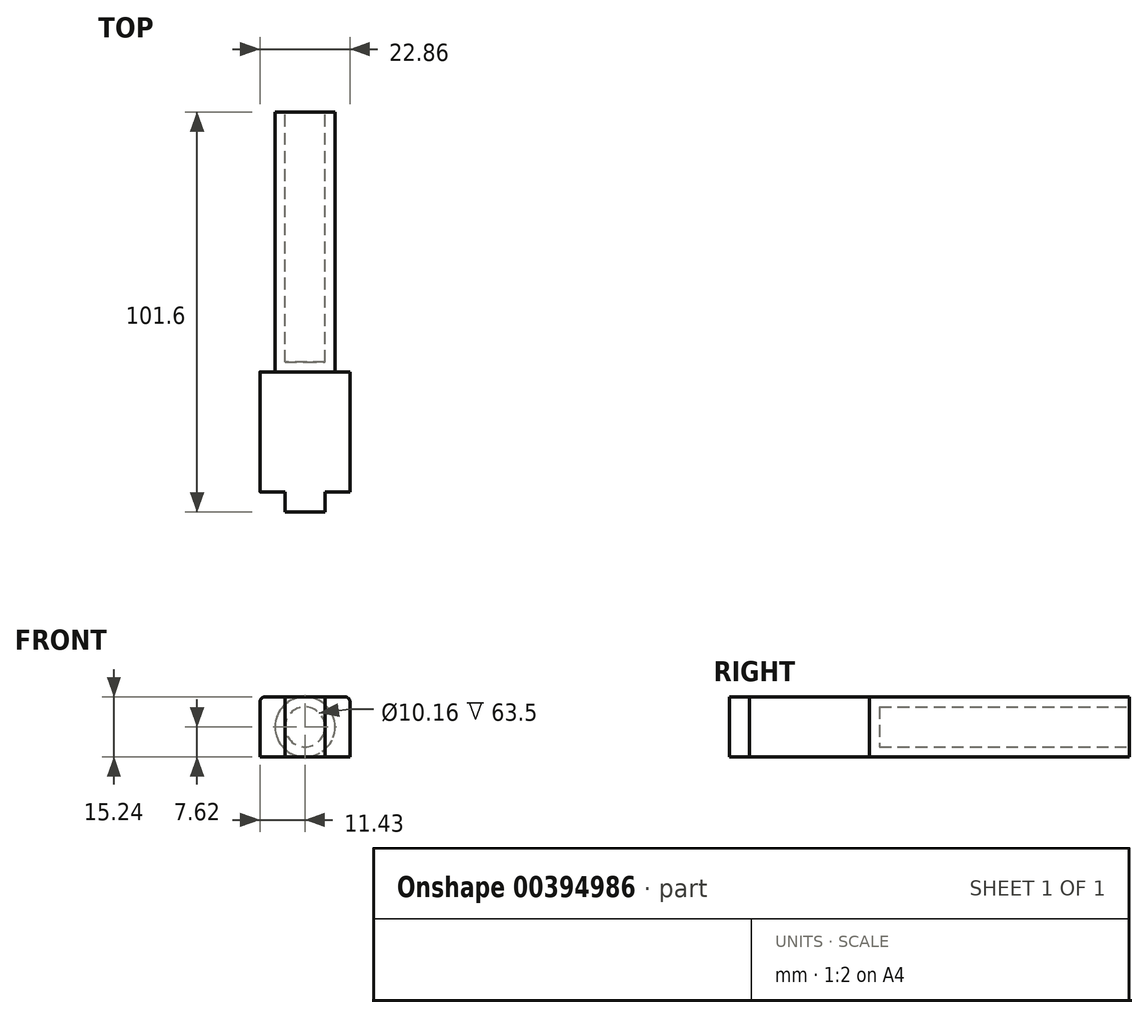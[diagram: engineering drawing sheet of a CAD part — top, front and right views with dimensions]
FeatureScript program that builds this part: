
annotation { "Feature Type Name" : "Feature", "Feature Type Description" : "" }
export const myFeature = defineFeature(function(context is Context, id is Id, definition is map)
    precondition{}
    {
        {
            var Q0;
            Q0=qCreatedBy(makeId("Right.planeOp"),FACE);
            var sketch = newSketch(context, id + "F0", { "sketchPlane" : qUnion([Q0])});
            skLineSegment(sketch, "E0.top", {"start": v(0, 12.7) * mm, "end": v(35.56, 12.7) * mm});
            skLineSegment(sketch, "E0.left", {"start": v(0, 0) * mm, "end": v(0, 12.7) * mm});
            skLineSegment(sketch, "E0.right", {"start": v(35.56, 0) * mm, "end": v(35.56, 12.7) * mm});
            skLineSegment(sketch, "E1.top", {"start": v(35.56, -2.54) * mm, "end": v(0, -2.54) * mm});
            skLineSegment(sketch, "E1.left", {"start": v(35.56, 0) * mm, "end": v(35.56, -2.54) * mm});
            skLineSegment(sketch, "E1.right", {"start": v(0, 0) * mm, "end": v(0, -2.54) * mm});
            skSolve(sketch);
        }
        {
            var Q0;
            Q0=makeQuery(id+"F0.imprint","IMPRINT",FACE,{"disambiguationData":[TD([[makeQuery(id+"F0.imprint","IMPRINT",EDGE,{"derivedFrom":sQuery(id+"F0.wireOp",EDGE,"E0.top")}),-1.0]])]});
            extrude(context, id + "F1", {"entities" : qUnion([Q0]), "endBound" : BoundingType.SYMMETRIC, "depth" : 22.86 * mm});
        }
        {
            var Q0;
            Q0=makeQuery(id+"F1.opExtrude","SWEPT_FACE",FACE,{"disambiguationData":[OSD([sQuery(id+"F0.wireOp",EDGE,"E0.top")])]});
            var sketch = newSketch(context, id + "F2", { "sketchPlane" : qUnion([Q0])});
            skLineSegment(sketch, "E2.bottom", {"start": v(-11.43, 0) * mm, "end": v(-5.08, 0) * mm});
            skLineSegment(sketch, "E2.top", {"start": v(-11.43, 5.08) * mm, "end": v(-5.08, 5.08) * mm});
            skLineSegment(sketch, "E2.left", {"start": v(-11.43, 0) * mm, "end": v(-11.43, 5.08) * mm});
            skLineSegment(sketch, "E2.right", {"start": v(-5.08, 0) * mm, "end": v(-5.08, 5.08) * mm});
            skLineSegment(sketch, "E3.bottom", {"start": v(11.43, 0) * mm, "end": v(5.08, 0) * mm});
            skLineSegment(sketch, "E3.top", {"start": v(11.43, 5.08) * mm, "end": v(5.08, 5.08) * mm});
            skLineSegment(sketch, "E3.left", {"start": v(11.43, 0) * mm, "end": v(11.43, 5.08) * mm});
            skLineSegment(sketch, "E3.right", {"start": v(5.08, 0) * mm, "end": v(5.08, 5.08) * mm});
            skSolve(sketch);
        }
        {
            var Q0;
            Q0 = qSketchRegion(id + "F2", true);
            extrude(context, id + "F3", {"entities" : qUnion([Q0]), "operationType" : NewBodyOperationType.REMOVE, "oppositeDirection" : true, "depth" : 25.4 * mm});
        }
        {
            var Q0;
            Q0=makeQuery(id+"F1.opExtrude","SWEPT_FACE",FACE,{"disambiguationData":[OSD([sQuery(id+"F0.wireOp",EDGE,"E0.right")])]});
            var sketch = newSketch(context, id + "F4", { "sketchPlane" : qUnion([Q0])});
            skCircle(sketch, "E4", {"center": v(0, 5.08) * mm, "radius": 7.62 * mm});
            skSolve(sketch);
        }
        {
            var Q0;
            Q0 = qSketchRegion(id + "F4", true);
            extrude(context, id + "F5", {"entities" : qUnion([Q0]), "operationType" : NewBodyOperationType.ADD, "depth" : 66.04 * mm});
        }
        {
            var Q0;
            Q0=makeQuery(id+"F5.opExtrude","CAP_FACE",FACE,{"disambiguationData":[OSD([sQuery(id+"F4.wireOp",EDGE,"E4")])],"isStart":false});
            var sketch = newSketch(context, id + "F6", { "sketchPlane" : qUnion([Q0])});
            skCircle(sketch, "E5", {"center": v(0, 5.08) * mm, "radius": 5.08 * mm});
            skSolve(sketch);
        }
        {
            var Q0;
            Q0=makeQuery(id+"F6.imprint","IMPRINT",FACE,{"disambiguationData":[TD([[makeQuery(id+"F6.imprint","IMPRINT",EDGE,{"derivedFrom":sQuery(id+"F6.wireOp",EDGE,"E5")}),1.0]])]});
            extrude(context, id + "F7", {"entities" : qUnion([Q0]), "operationType" : NewBodyOperationType.REMOVE, "oppositeDirection" : true, "depth" : 63.5 * mm});
        }
        {
            var Q0;
            Q0=makeQuery(id+"F1.opExtrude","CAP_EDGE",EDGE,{"disambiguationData":[OSD([sQuery(id+"F0.wireOp",EDGE,"E0.top")])],"isStart":true});
            var Q1;
            Q1=makeQuery(id+"F1.opExtrude","CAP_EDGE",EDGE,{"disambiguationData":[OSD([sQuery(id+"F0.wireOp",EDGE,"E0.top")])],"isStart":false});
            fillet(context, id + "F8", {"entities" : qUnion([Q0, Q1]), "radius" : 1.27 * mm, "tangentPropagation" : true, "allowEdgeOverflow" : false});
        }
    });
